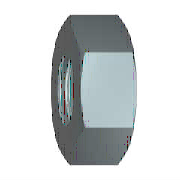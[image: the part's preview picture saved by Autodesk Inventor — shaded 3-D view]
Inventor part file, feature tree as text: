
AUTODESK INVENTOR PART (.ipt)
format: ipt  version: 2021 (Build 250183000, 183)  size: 167,424 bytes
history: native  units: mm (DEFAULTED — no unit token found)
features: sketch x3, chamfer x1, hole x1, other x1, plane x1
ambient origin geometry x7: Origin, YZ Plane, XZ Plane, X Axis, Y Axis, Z Axis, Center Point
bodies: Solid1 (feature_tree), Body (feature_tree)
feature tree (7):
  chamfer  "Chamfer1"  Angle=30.0deg  [1 undecoded]
  hole  "Thread"  [1 undecoded]
  other  "Work Axis1"
  plane  "Work Plane1"
  sketch  "Sketch1"  dims[d0=6.350853mm]
  sketch  "Sketch2"  dims[d1=2.4mm]
  sketch  "Sketch3"  dims[d2=0.0mm d3=30.0deg d4=30.0deg d5=4.5mm d6=4.5mm d7=90.0deg d25=2.459mm d26=6.0mm d27=4.0mm d28=2.0mm d29=14.3117mm d30=8.0mm d31=20.594885mm d8=0.270633mm d9=30.0deg d10=0.270633mm d11=30.0deg d13=0.0mm d14=0.0mm d39=0.0mm d40=0.270633mm d41=0.270633mm d42=0.0mm]
note: 2 required parameter values undecoded (feature->parameter linkage not recoverable at this tier; creation-order binding heuristic only, values carry confidence <= 0.55)
